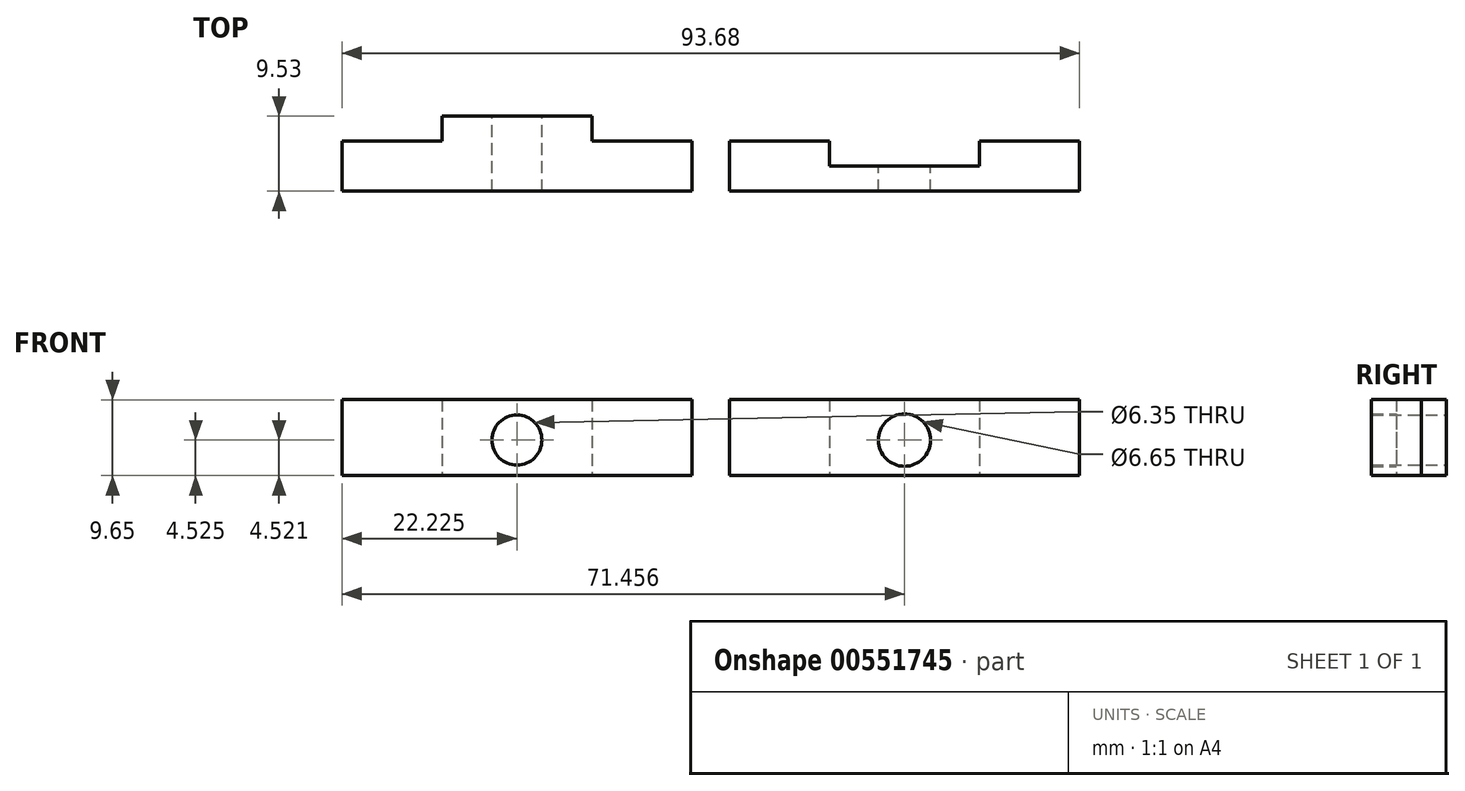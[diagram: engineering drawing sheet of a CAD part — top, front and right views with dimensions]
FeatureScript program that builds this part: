
annotation { "Feature Type Name" : "Feature", "Feature Type Description" : "" }
export const myFeature = defineFeature(function(context is Context, id is Id, definition is map)
    precondition{}
    {
        {
            var Q0;
            Q0=qCreatedBy(makeId("Top.planeOp"),FACE);
            var sketch = newSketch(context, id + "F0", { "sketchPlane" : qUnion([Q0])});
            skLineSegment(sketch, "E0.bottom", {"start": v(6.64, 6.35) * mm, "end": v(19.34, 6.35) * mm});
            skLineSegment(sketch, "E0.top", {"start": v(6.64, 0) * mm, "end": v(51.1, 0) * mm});
            skLineSegment(sketch, "E0.left", {"start": v(6.64, 6.35) * mm, "end": v(6.64, 0) * mm});
            skLineSegment(sketch, "E0.right", {"start": v(51.1, 6.35) * mm, "end": v(51.1, 0) * mm});
            skLineSegment(sketch, "E1.top", {"start": v(19.34, 3.17) * mm, "end": v(38.4, 3.17) * mm});
            skLineSegment(sketch, "E1.left", {"start": v(19.34, 6.35) * mm, "end": v(19.34, 3.17) * mm});
            skLineSegment(sketch, "E1.right", {"start": v(38.4, 6.35) * mm, "end": v(38.4, 3.17) * mm});
            skLineSegment(sketch, "E2.trimOffspring", {"start": v(38.4, 6.35) * mm, "end": v(51.1, 6.35) * mm});
            skLineSegment(sketch, "E3.bottom", {"start": v(-42.59, 6.35) * mm, "end": v(-29.89, 6.35) * mm});
            skLineSegment(sketch, "E3.top", {"start": v(-42.59, 0) * mm, "end": v(1.86, 0) * mm});
            skLineSegment(sketch, "E3.left", {"start": v(-42.59, 6.35) * mm, "end": v(-42.59, 0) * mm});
            skLineSegment(sketch, "E3.right", {"start": v(1.86, 6.35) * mm, "end": v(1.86, 0) * mm});
            skLineSegment(sketch, "E4.bottom", {"start": v(-29.89, 9.52) * mm, "end": v(-10.84, 9.52) * mm});
            skLineSegment(sketch, "E4.left", {"start": v(-29.89, 9.52) * mm, "end": v(-29.89, 6.35) * mm});
            skLineSegment(sketch, "E4.right", {"start": v(-10.84, 9.52) * mm, "end": v(-10.84, 6.35) * mm});
            skLineSegment(sketch, "E5.trimOffspring", {"start": v(-10.84, 6.35) * mm, "end": v(1.86, 6.35) * mm});
            skSolve(sketch);
        }
        {
            var Q0;
            Q0=makeQuery(id+"F0.imprint","IMPRINT",FACE,{"disambiguationData":[TD([[makeQuery(id+"F0.imprint","IMPRINT",EDGE,{"derivedFrom":sQuery(id+"F0.wireOp",EDGE,"E0.bottom")}),-1.0]])]});
            extrude(context, id + "F1", {"entities" : qUnion([Q0]), "depth" : 9.65 * mm, "offsetDistance" : 25.4 * mm});
        }
        {
            var Q0;
            Q0 = qSketchRegion(id + "F0", true);
            extrude(context, id + "F2", {"entities" : qUnion([Q0]), "operationType" : NewBodyOperationType.ADD, "depth" : 9.65 * mm, "offsetDistance" : 25.4 * mm});
        }
        {
            var Q0;
            Q0=makeQuery(id+"F2.opExtrude","SWEPT_FACE",FACE,{"disambiguationData":[OSD([sQuery(id+"F0.wireOp",EDGE,"E4.bottom")])]});
            var sketch = newSketch(context, id + "F3", { "sketchPlane" : qUnion([Q0])});
            skCircle(sketch, "E6", {"center": v(20.36, 4.53) * mm, "radius": 3.18 * mm});
            skSolve(sketch);
        }
        {
            var Q0;
            Q0 = qSketchRegion(id + "F3", true);
            extrude(context, id + "F4", {"entities" : qUnion([Q0]), "operationType" : NewBodyOperationType.REMOVE, "oppositeDirection" : true, "depth" : 25.4 * mm, "offsetDistance" : 25.4 * mm});
        }
        {
            var Q0;
            Q0=makeQuery(id+"F1.opExtrude","SWEPT_FACE",FACE,{"disambiguationData":[OSD([sQuery(id+"F0.wireOp",EDGE,"E1.top")])]});
            var sketch = newSketch(context, id + "F5", { "sketchPlane" : qUnion([Q0])});
            skCircle(sketch, "E7", {"center": v(-28.87, 4.52) * mm, "radius": 3.33 * mm});
            skSolve(sketch);
        }
        {
            var Q0;
            Q0=makeQuery(id+"F5.imprint","IMPRINT",FACE,{"disambiguationData":[TD([[makeQuery(id+"F5.imprint","IMPRINT",EDGE,{"derivedFrom":sQuery(id+"F5.wireOp",EDGE,"E7")}),1.0]])]});
            var Q1;
            Q1=sQuery(id+"F5.wireOp",EDGE,"E7");
            extrude(context, id + "F6", {"entities" : qUnion([Q0]), "operationType" : NewBodyOperationType.REMOVE, "surfaceEntities" : qUnion([Q1]), "oppositeDirection" : true, "depth" : 25.4 * mm, "offsetDistance" : 25.4 * mm});
        }
    });
